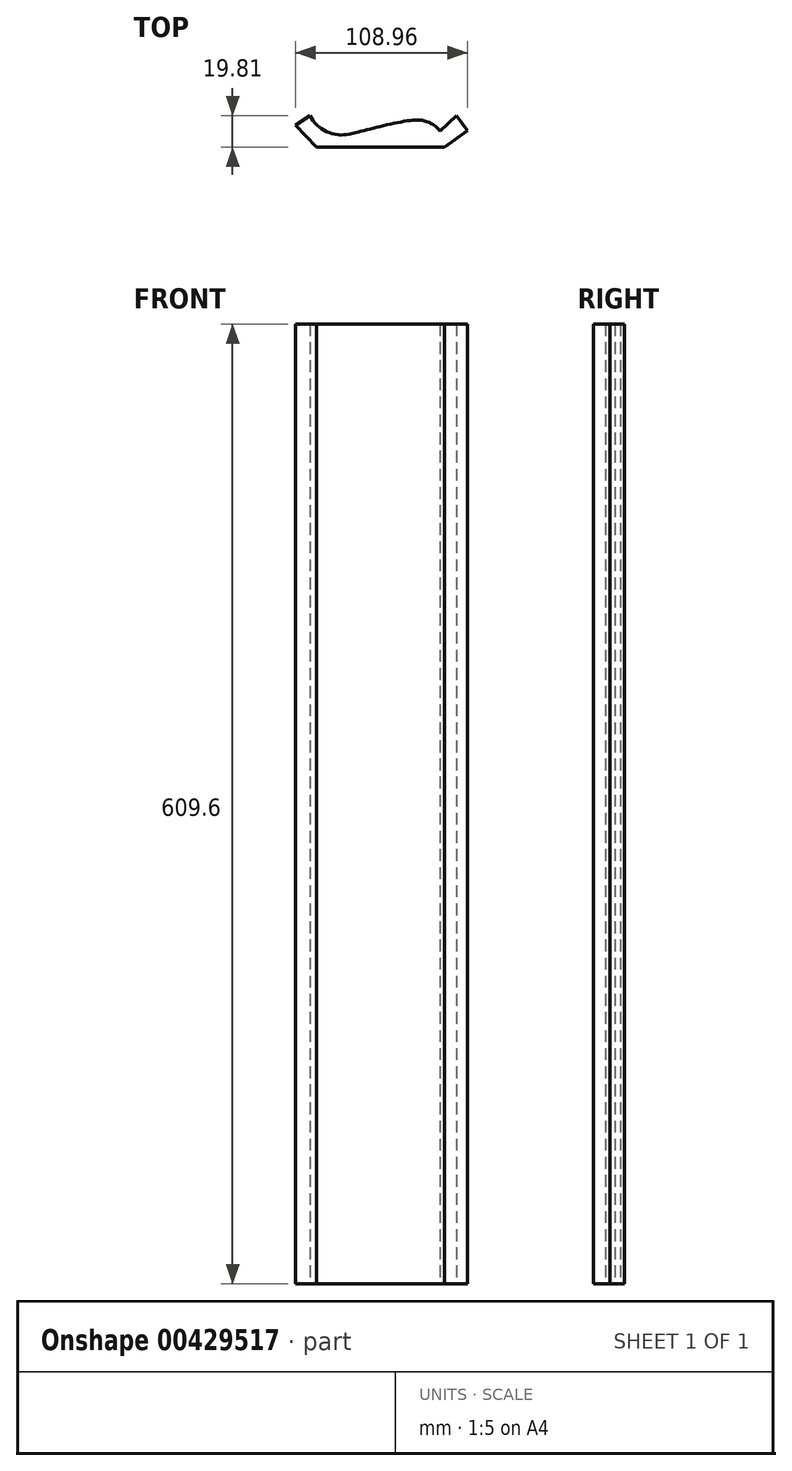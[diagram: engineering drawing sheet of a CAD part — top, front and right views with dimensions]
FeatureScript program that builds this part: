
annotation { "Feature Type Name" : "Feature", "Feature Type Description" : "" }
export const myFeature = defineFeature(function(context is Context, id is Id, definition is map)
    precondition{}
    {
        {
            var Q0;
            Q0=qCreatedBy(makeId("Top.planeOp"),FACE);
            var sketch = newSketch(context, id + "F0", { "sketchPlane" : qUnion([Q0])});
            skLineSegment(sketch, "E0", {"start": v(0, 0) * mm, "end": v(81.28, 0) * mm});
            skLineSegment(sketch, "E1", {"start": v(81.28, 0) * mm, "end": v(95.65, 10.44) * mm});
            skLineSegment(sketch, "E2", {"start": v(95.65, 10.44) * mm, "end": v(88.84, 19.81) * mm});
            skLineSegment(sketch, "E3", {"start": v(88.84, 19.81) * mm, "end": v(78.4, 10.16) * mm});
            skLineSegment(sketch, "E4", {"start": v(0, 0) * mm, "end": v(-13.31, 13.79) * mm});
            skLineSegment(sketch, "E5", {"start": v(-13.31, 13.79) * mm, "end": v(-4.27, 19.81) * mm});
            skArc(sketch, "E6", {"start": v(-4.27, 19.81) * mm, "mid": v(6.34, 9.74) * mm, "end": v(20.88, 8.16) * mm});
            skArc(sketch, "E7", {"start": v(78.4, 10.16) * mm, "mid": v(69.9, 16.1) * mm, "end": v(59.54, 16.7) * mm});
            skLineSegment(sketch, "E8", {"start": v(20.88, 8.16) * mm, "end": v(59.54, 16.7) * mm, "construction": true});
            skFitSpline(sketch, "E9", {"points": [v(20.88, 8.16) * mm, v(63.65, 17.15) * mm], "startDerivative": vector(22.9, 5.06) * mm, "endDerivative": vector(29.36, 0) * mm});
            skSolve(sketch);
        }
        {
            var Q0;
            Q0 = qSketchRegion(id + "F0", true);
            extrude(context, id + "F1", {"entities" : qUnion([Q0]), "depth" : 609.6 * mm});
        }
    });
